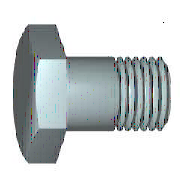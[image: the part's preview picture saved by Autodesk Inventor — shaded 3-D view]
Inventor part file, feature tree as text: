
AUTODESK INVENTOR PART (.ipt)
format: ipt  version: 2021 (Build 250183000, 183)  size: 193,536 bytes
history: native  units: mm (DEFAULTED — no unit token found)
features: sketch x3, extrude x1, chamfer x1, plane x1
ambient origin geometry x7: Origin, YZ Plane, XZ Plane, X Axis, Y Axis, Z Axis, Center Point
bodies: Solid1 (feature_tree), Body (feature_tree)
feature tree (6):
  extrude  "Head"  Depth=26.0mm
  chamfer  "Chamfer1"  Distance=5.8mm
  plane  "Work Plane1"
  sketch  "Sketch1"  dims[d0=45.0mm d1=26.0mm]
  sketch  "Sketch2"  dims[d2=10.0mm]
  sketch  "Sketch4"  dims[d12=90.0deg d3=5.8mm d4=0.0mm d5=30.0deg d21=90.0deg d6=0.920175mm d7=0.920275mm d8=0.0mm d9=0.6001mm d10=14.63mm d11=16.0mm d13=0.920275mm d14=10.0mm d15=26.0mm d16=0.0mm d19=16.0mm d55=45.0deg d57=0.0mm d58=0.0mm]
